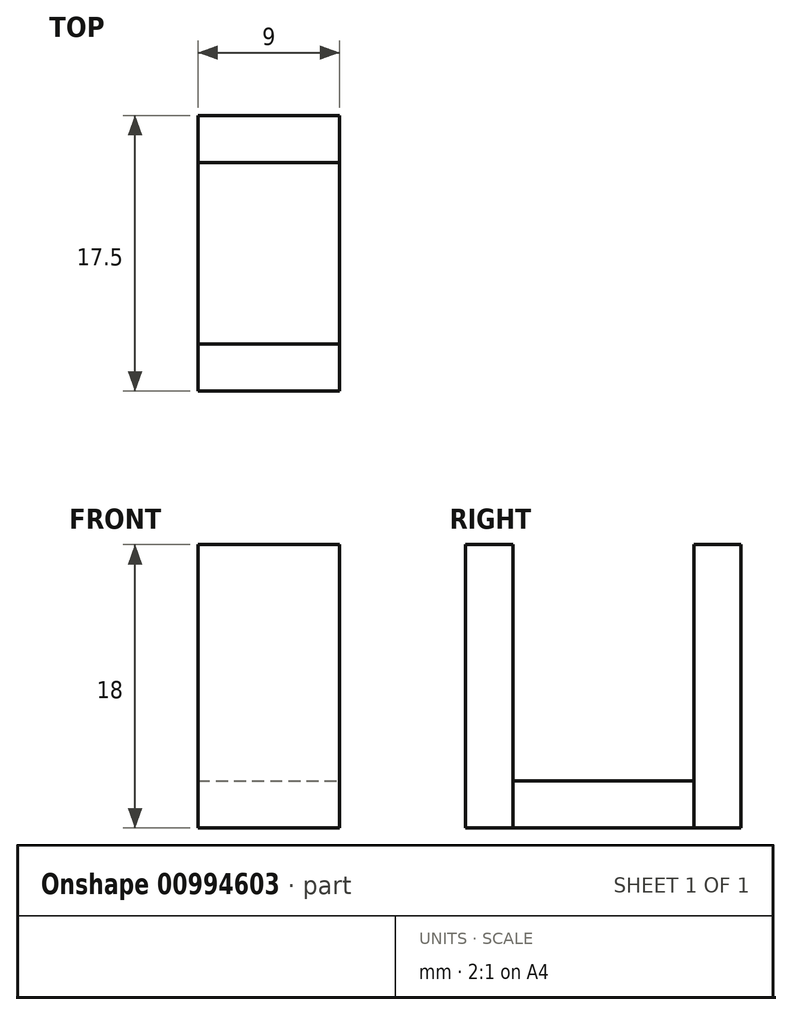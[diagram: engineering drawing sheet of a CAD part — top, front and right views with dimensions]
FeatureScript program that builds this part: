
annotation { "Feature Type Name" : "Feature", "Feature Type Description" : "" }
export const myFeature = defineFeature(function(context is Context, id is Id, definition is map)
    precondition{}
    {
        {
            var Q0;
            Q0=qCreatedBy(makeId("Top.planeOp"),FACE);
            var sketch = newSketch(context, id + "F0", { "sketchPlane" : qUnion([Q0])});
            skLineSegment(sketch, "E0.bottom", {"start": v(-41.72, 0) * mm, "end": v(-32.72, 0) * mm});
            skLineSegment(sketch, "E0.top", {"start": v(-41.72, -17.5) * mm, "end": v(-32.72, -17.5) * mm});
            skLineSegment(sketch, "E0.left", {"start": v(-41.72, 0) * mm, "end": v(-41.72, -17.5) * mm});
            skLineSegment(sketch, "E0.right", {"start": v(-32.72, 0) * mm, "end": v(-32.72, -17.5) * mm});
            skLineSegment(sketch, "E1", {"start": v(-41.72, -14.5) * mm, "end": v(-32.72, -14.5) * mm});
            skLineSegment(sketch, "E2", {"start": v(-41.72, -3) * mm, "end": v(-32.72, -3) * mm});
            skSolve(sketch);
        }
        {
            var Q0;
            {var subQ0=sQuery(id+"F0.wireOp",EDGE,"E0.bottom");Q0=makeQuery(id+"F0.imprint","IMPRINT",FACE,{"disambiguationData":[TD([[makeQuery(id+"F0.imprint","IMPRINT",EDGE,{"derivedFrom":subQ0}),-1.0]])]});}
            var Q1;
            {var subQ0=sQuery(id+"F0.wireOp",EDGE,"E0.top");Q1=makeQuery(id+"F0.imprint","IMPRINT",FACE,{"disambiguationData":[TD([[makeQuery(id+"F0.imprint","IMPRINT",EDGE,{"derivedFrom":subQ0}),1.0]])]});}
            extrude(context, id + "F1", {"entities" : qUnion([Q0, Q1]), "depth" : 18 * mm, "offsetDistance" : 25 * mm});
        }
        {
            var Q0;
            {var subQ0=sQuery(id+"F0.wireOp",EDGE,"E1");Q0=makeQuery(id+"F0.imprint","IMPRINT",FACE,{"disambiguationData":[TD([[makeQuery(id+"F0.imprint","IMPRINT",EDGE,{"derivedFrom":subQ0}),1.0]])]});}
            extrude(context, id + "F2", {"entities" : qUnion([Q0]), "depth" : 3 * mm, "offsetDistance" : 25 * mm});
        }
    });
